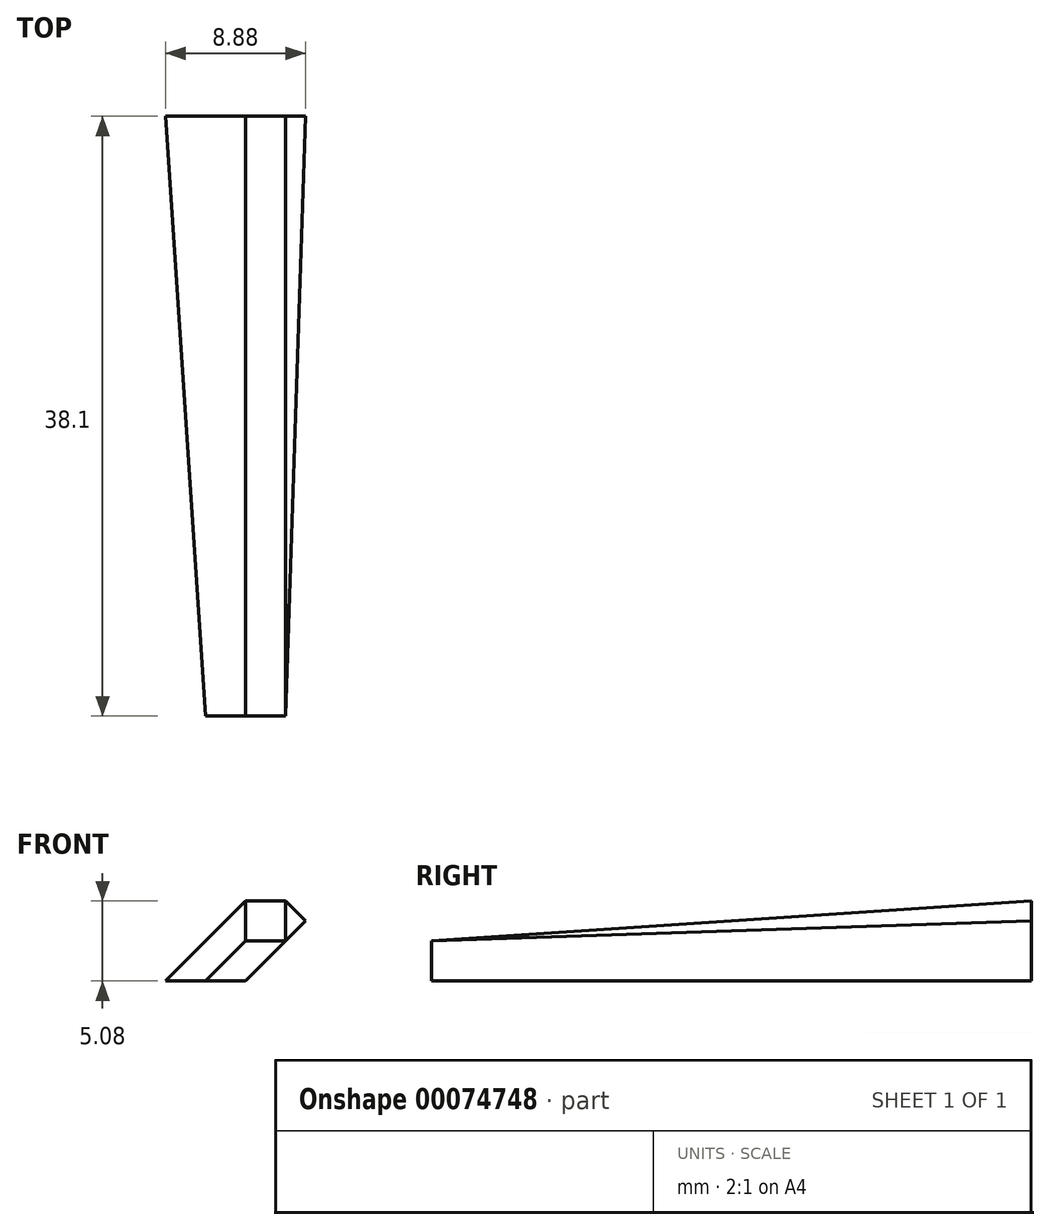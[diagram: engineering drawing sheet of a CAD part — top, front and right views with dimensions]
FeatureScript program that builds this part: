
annotation { "Feature Type Name" : "Feature", "Feature Type Description" : "" }
export const myFeature = defineFeature(function(context is Context, id is Id, definition is map)
    precondition{}
    {
        {
            var Q0;
            Q0=qCreatedBy(makeId("Front.planeOp"),FACE);
            var sketch = newSketch(context, id + "F0", { "sketchPlane" : qUnion([Q0])});
            skLineSegment(sketch, "E0", {"start": v(0, 0) * mm, "end": v(10.16, 0) * mm});
            skLineSegment(sketch, "E1", {"start": v(0, 0) * mm, "end": v(0, 5.08) * mm});
            skLineSegment(sketch, "E2", {"start": v(10.16, 0) * mm, "end": v(10.16, 5.08) * mm});
            skLineSegment(sketch, "E3", {"start": v(0, 5.08) * mm, "end": v(10.16, 5.08) * mm});
            skSolve(sketch);
        }
        {
            var Q0;
            Q0=makeQuery(id+"F0.imprint","IMPRINT",FACE,{"disambiguationData":[TD([[makeQuery(id+"F0.imprint","IMPRINT",EDGE,{"derivedFrom":sQuery(id+"F0.wireOp",EDGE,"E0")}),1.0]])]});
            extrude(context, id + "F1", {"entities" : qUnion([Q0]), "depth" : 38.1 * mm});
        }
        {
            var Q0;
            Q0=makeQuery(id+"F1.opExtrude","CAP_EDGE",EDGE,{"disambiguationData":[OSD([sQuery(id+"F0.wireOp",EDGE,"E3")])],"isStart":false});
            chamfer(context, id + "F2", {"entities" : qUnion([Q0]), "chamferType" : ChamferType.TWO_OFFSETS, "width1" : 38.1 * mm, "oppositeDirection" : false, "width2" : 2.54 * mm, "tangentPropagation" : true});
        }
        {
            var Q0;
            Q0=makeQuery(id+"F2.opChamfer","BLEND_EDGE",EDGE,{"blendedFrom":[makeQuery(id+"F1.opExtrude","CAP_EDGE",EDGE,{"disambiguationData":[OSD([sQuery(id+"F0.wireOp",EDGE,"E3")])],"isStart":false}),makeQuery(id+"F1.opExtrude","SWEPT_FACE",FACE,{"disambiguationData":[OSD([sQuery(id+"F0.wireOp",EDGE,"E1")])]})],"blendedInto":[makeQuery(id+"F1.opExtrude","SWEPT_FACE",FACE,{"disambiguationData":[OSD([sQuery(id+"F0.wireOp",EDGE,"E1")])]})]});
            chamfer(context, id + "F3", {"entities" : qUnion([Q0]), "width" : 5.08 * mm, "tangentPropagation" : true});
        }
        {
            var Q0;
            Q0=makeQuery(id+"F2.opChamfer","BLEND_EDGE",EDGE,{"blendedFrom":[makeQuery(id+"F1.opExtrude","CAP_EDGE",EDGE,{"disambiguationData":[OSD([sQuery(id+"F0.wireOp",EDGE,"E3")])],"isStart":false}),makeQuery(id+"F1.opExtrude","SWEPT_FACE",FACE,{"disambiguationData":[OSD([sQuery(id+"F0.wireOp",EDGE,"E2")])]})],"blendedInto":[makeQuery(id+"F1.opExtrude","SWEPT_FACE",FACE,{"disambiguationData":[OSD([sQuery(id+"F0.wireOp",EDGE,"E2")])]})]});
            chamfer(context, id + "F4", {"entities" : qUnion([Q0]), "width" : 2.54 * mm, "tangentPropagation" : true});
        }
        {
            var Q0;
            Q0=makeQuery(id+"F1.opExtrude","SWEPT_EDGE",EDGE,{"disambiguationData":[OSD([sQuery(id+"F0.wireOp",EDGE,"E0"),sQuery(id+"F0.wireOp",EDGE,"E2")])]});
            chamfer(context, id + "F5", {"entities" : qUnion([Q0]), "width" : 5.08 * mm, "tangentPropagation" : true});
        }
    });
